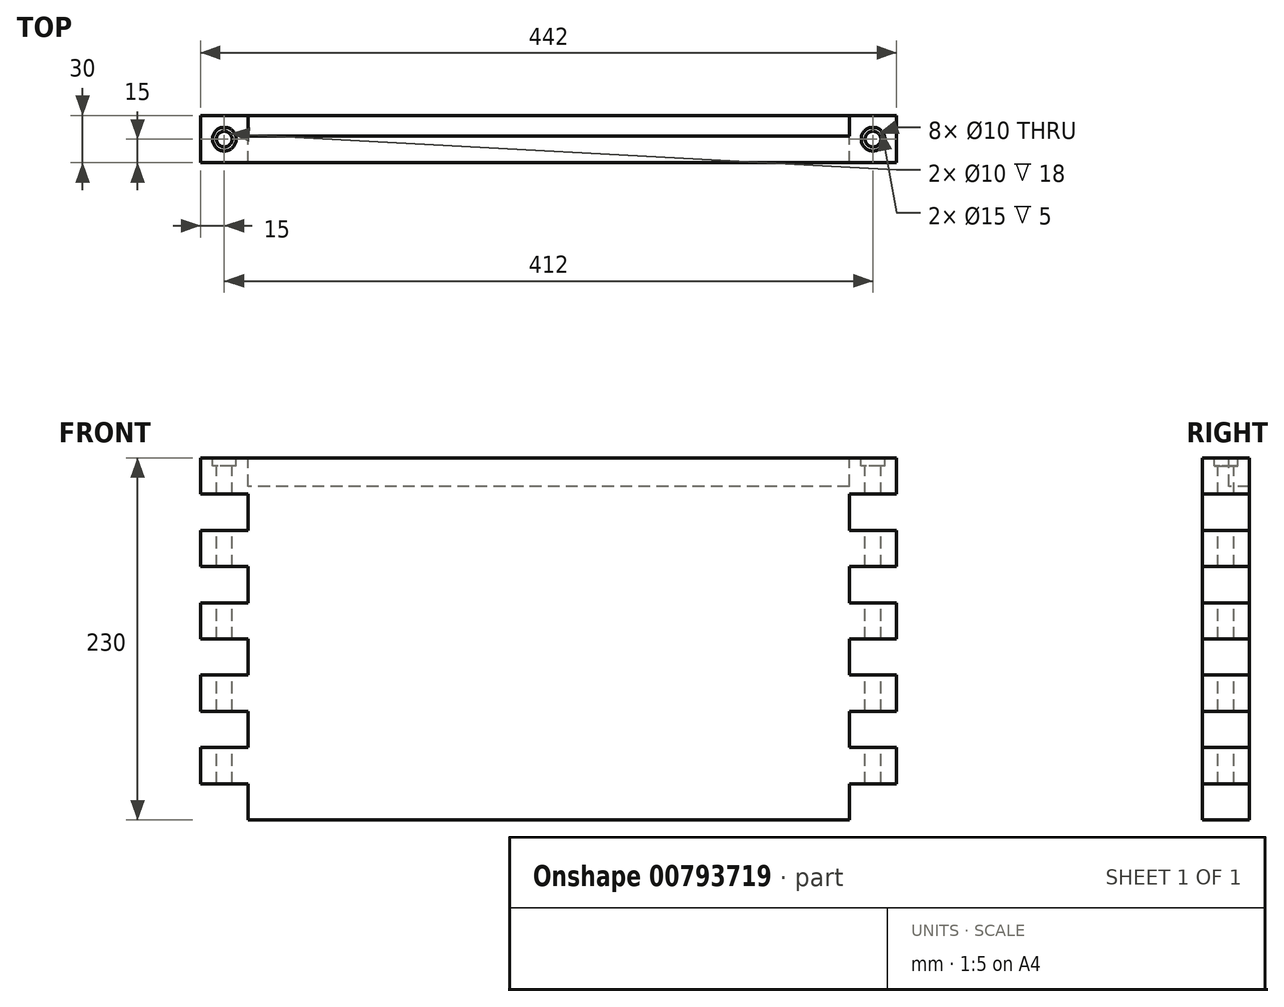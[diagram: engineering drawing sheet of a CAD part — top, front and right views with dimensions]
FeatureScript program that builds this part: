
annotation { "Feature Type Name" : "Feature", "Feature Type Description" : "" }
export const myFeature = defineFeature(function(context is Context, id is Id, definition is map)
    precondition{}
    {
        {
            var Q0;
            Q0=qCreatedBy(makeId("Front.planeOp"),FACE);
            var sketch = newSketch(context, id + "F0", { "sketchPlane" : qUnion([Q0])});
            skLineSegment(sketch, "E0.bottom", {"start": v(221, 115) * mm, "end": v(-221, 115) * mm});
            skLineSegment(sketch, "E0.top", {"start": v(221, -115) * mm, "end": v(-221, -115) * mm});
            skLineSegment(sketch, "E0.left", {"start": v(221, 115) * mm, "end": v(221, -115) * mm});
            skLineSegment(sketch, "E0.right", {"start": v(-221, 115) * mm, "end": v(-221, -115) * mm});
            skPoint(sketch, "E0.middle", {"position": v(0, 0) * mm});
            skLineSegment(sketch, "E1.bottom", {"start": v(-191, 92) * mm, "end": v(-221, 92) * mm});
            skLineSegment(sketch, "E1.top", {"start": v(-191, 69) * mm, "end": v(-221, 69) * mm});
            skLineSegment(sketch, "E1.left", {"start": v(-191, 92) * mm, "end": v(-191, 69) * mm});
            skLineSegment(sketch, "E1.right", {"start": v(-221, 92) * mm, "end": v(-221, 69) * mm});
            skLineSegment(sketch, "E2.MirrorCS", {"start": v(-191, 46) * mm, "end": v(-221, 46) * mm});
            skLineSegment(sketch, "E3.MirrorCS", {"start": v(-191, 23) * mm, "end": v(-221, 23) * mm});
            skLineSegment(sketch, "E4.MirrorCS", {"start": v(-191, 0) * mm, "end": v(-221, 0) * mm});
            skLineSegment(sketch, "E5.MirrorCS", {"start": v(-191, -23) * mm, "end": v(-221, -23) * mm});
            skLineSegment(sketch, "E6.MirrorCS", {"start": v(-191, -46) * mm, "end": v(-221, -46) * mm});
            skLineSegment(sketch, "E7.MirrorCS", {"start": v(-191, -69) * mm, "end": v(-221, -69) * mm});
            skLineSegment(sketch, "E8.MirrorCS", {"start": v(-191, -92) * mm, "end": v(-221, -92) * mm});
            skLineSegment(sketch, "E9.MirrorCS", {"start": v(191, 92) * mm, "end": v(221, 92) * mm});
            skLineSegment(sketch, "E10.MirrorCS", {"start": v(191, 69) * mm, "end": v(221, 69) * mm});
            skLineSegment(sketch, "E11.MirrorCS", {"start": v(191, 46) * mm, "end": v(221, 46) * mm});
            skLineSegment(sketch, "E12.MirrorCS", {"start": v(191, 23) * mm, "end": v(221, 23) * mm});
            skLineSegment(sketch, "E13.MirrorCS", {"start": v(191, 0) * mm, "end": v(221, 0) * mm});
            skLineSegment(sketch, "E14.MirrorCS", {"start": v(191, -23) * mm, "end": v(221, -23) * mm});
            skLineSegment(sketch, "E15.MirrorCS", {"start": v(191, -46) * mm, "end": v(221, -46) * mm});
            skLineSegment(sketch, "E16.MirrorCS", {"start": v(191, -69) * mm, "end": v(221, -69) * mm});
            skLineSegment(sketch, "E17.MirrorCS", {"start": v(191, -92) * mm, "end": v(221, -92) * mm});
            skLineSegment(sketch, "E18", {"start": v(-191, 46) * mm, "end": v(-191, 23) * mm});
            skLineSegment(sketch, "E19", {"start": v(-191, 0) * mm, "end": v(-191, -23) * mm});
            skLineSegment(sketch, "E20", {"start": v(-191, -46) * mm, "end": v(-191, -69) * mm});
            skLineSegment(sketch, "E21", {"start": v(-191, -92) * mm, "end": v(-191, -115) * mm});
            skLineSegment(sketch, "E22", {"start": v(191, 92) * mm, "end": v(191, 69) * mm});
            skLineSegment(sketch, "E23", {"start": v(191, 46) * mm, "end": v(191, 23) * mm});
            skLineSegment(sketch, "E24", {"start": v(191, 0) * mm, "end": v(191, -23) * mm});
            skLineSegment(sketch, "E25", {"start": v(191, -46) * mm, "end": v(191, -69) * mm});
            skLineSegment(sketch, "E26", {"start": v(191, -92) * mm, "end": v(191, -115) * mm});
            skSolve(sketch);
        }
        {
            var Q0;
            {var subQ18=sQuery(id+"F0.wireOp",EDGE,"E0.bottom");Q0=makeQuery(id+"F0.imprint","IMPRINT",FACE,{"disambiguationData":[TD([[makeQuery(id+"F0.imprint","IMPRINT",EDGE,{"derivedFrom":subQ18}),1.0]])]});}
            extrude(context, id + "F1", {"entities" : qUnion([Q0]), "depth" : 30 * mm, "offsetDistance" : 25 * mm});
        }
        {
            var Q0;
            Q0=makeQuery(id+"F1.opExtrude","SWEPT_FACE",FACE,{"disambiguationData":[OSD([sQuery(id+"F0.wireOp",EDGE,"E0.bottom")])]});
            var sketch = newSketch(context, id + "F2", { "sketchPlane" : qUnion([Q0])});
            skPoint(sketch, "E27", {"position": v(-206, -15) * mm});
            skPoint(sketch, "E28.MirrorP", {"position": v(206, -15) * mm});
            skLineSegment(sketch, "E29.bottom", {"start": v(-191, 0) * mm, "end": v(191, 0) * mm});
            skLineSegment(sketch, "E29.top", {"start": v(-191, -13) * mm, "end": v(191, -13) * mm});
            skLineSegment(sketch, "E29.left", {"start": v(-191, 0) * mm, "end": v(-191, -13) * mm});
            skLineSegment(sketch, "E29.right", {"start": v(191, 0) * mm, "end": v(191, -13) * mm});
            skSolve(sketch);
        }
        {
            var Q0;
            Q0=sQuery(id+"F2.wireOp",VERTEX,"E27");
            var Q1;
            Q1=sQuery(id+"F2.wireOp",VERTEX,"E28.MirrorP");
            var Q2;
            Q2=makeQuery(id+"F1.opExtrude","SWEPT_BODY",BODY,{"disambiguationData":[OSD([sQuery(id+"F0.wireOp",EDGE,"E0.bottom"),sQuery(id+"F0.wireOp",EDGE,"E0.top"),sQuery(id+"F0.wireOp",EDGE,"E0.left"),sQuery(id+"F0.wireOp",EDGE,"E0.right"),sQuery(id+"F0.wireOp",EDGE,"E1.bottom"),sQuery(id+"F0.wireOp",EDGE,"E1.top"),sQuery(id+"F0.wireOp",EDGE,"E1.left"),sQuery(id+"F0.wireOp",EDGE,"E2.MirrorCS"),sQuery(id+"F0.wireOp",EDGE,"E3.MirrorCS"),sQuery(id+"F0.wireOp",EDGE,"E4.MirrorCS"),sQuery(id+"F0.wireOp",EDGE,"E5.MirrorCS"),sQuery(id+"F0.wireOp",EDGE,"E6.MirrorCS"),sQuery(id+"F0.wireOp",EDGE,"E7.MirrorCS"),sQuery(id+"F0.wireOp",EDGE,"E8.MirrorCS"),sQuery(id+"F0.wireOp",EDGE,"E9.MirrorCS"),sQuery(id+"F0.wireOp",EDGE,"E10.MirrorCS"),sQuery(id+"F0.wireOp",EDGE,"E11.MirrorCS"),sQuery(id+"F0.wireOp",EDGE,"E12.MirrorCS"),sQuery(id+"F0.wireOp",EDGE,"E13.MirrorCS"),sQuery(id+"F0.wireOp",EDGE,"E14.MirrorCS"),sQuery(id+"F0.wireOp",EDGE,"E15.MirrorCS"),sQuery(id+"F0.wireOp",EDGE,"E16.MirrorCS"),sQuery(id+"F0.wireOp",EDGE,"E17.MirrorCS"),sQuery(id+"F0.wireOp",EDGE,"E18"),sQuery(id+"F0.wireOp",EDGE,"E19"),sQuery(id+"F0.wireOp",EDGE,"E20"),sQuery(id+"F0.wireOp",EDGE,"E21"),sQuery(id+"F0.wireOp",EDGE,"E22"),sQuery(id+"F0.wireOp",EDGE,"E23"),sQuery(id+"F0.wireOp",EDGE,"E24"),sQuery(id+"F0.wireOp",EDGE,"E25"),sQuery(id+"F0.wireOp",EDGE,"E26")])]});
            hole(context, id + "F3", {"style" : HoleStyle.C_BORE, "endStyle" : HoleEndStyle.THROUGH, "holeDiameter" : 10 * mm, "cBoreDiameter" : 15 * mm, "cBoreDepth" : 5 * mm, "majorDiameter" : 5 * mm, "isTappedThrough" : true, "tappedDepth" : 12 * mm, "tapClearance" : 3, "locations" : qUnion([Q0, Q1]), "scope" : qUnion([Q2])});
        }
        {
            var Q0;
            Q0=makeQuery(id+"F2.imprint","IMPRINT",FACE,{"disambiguationData":[TD([[makeQuery(id+"F2.imprint","IMPRINT",EDGE,{"derivedFrom":sQuery(id+"F2.wireOp",EDGE,"E29.bottom")}),1.0]])]});
            extrude(context, id + "F4", {"entities" : qUnion([Q0]), "operationType" : NewBodyOperationType.REMOVE, "oppositeDirection" : true, "depth" : 18 * mm, "offsetDistance" : 25 * mm});
        }
    });
